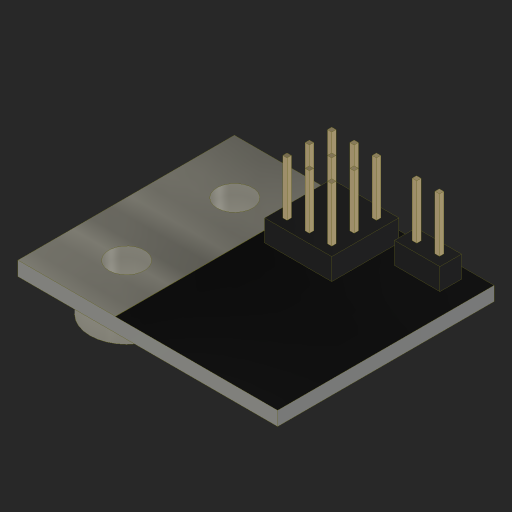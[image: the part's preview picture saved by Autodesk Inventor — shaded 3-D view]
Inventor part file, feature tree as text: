
AUTODESK INVENTOR PART (.ipt)
format: ipt  version: 2023 (Build 270158000, 158)  size: 308,736 bytes
history: native  units: in
note: dims shown in document units (in); Inventor stores cm internally (conversion verified against a paired STEP export)
features: extrude x1, imported_body x1
ambient origin geometry x8: Origin, YZ Plane, XZ Plane, XY Plane, X Axis, Y Axis, Z Axis, Center Point
bodies: Body1 (feature_tree)
feature tree (2):
  extrude  "Extrude6"  [1 undecoded]
  imported_body  "Base1"
note: 1 required parameter value undecoded (feature->parameter linkage not recoverable at this tier; creation-order binding heuristic only, values carry confidence <= 0.55)
